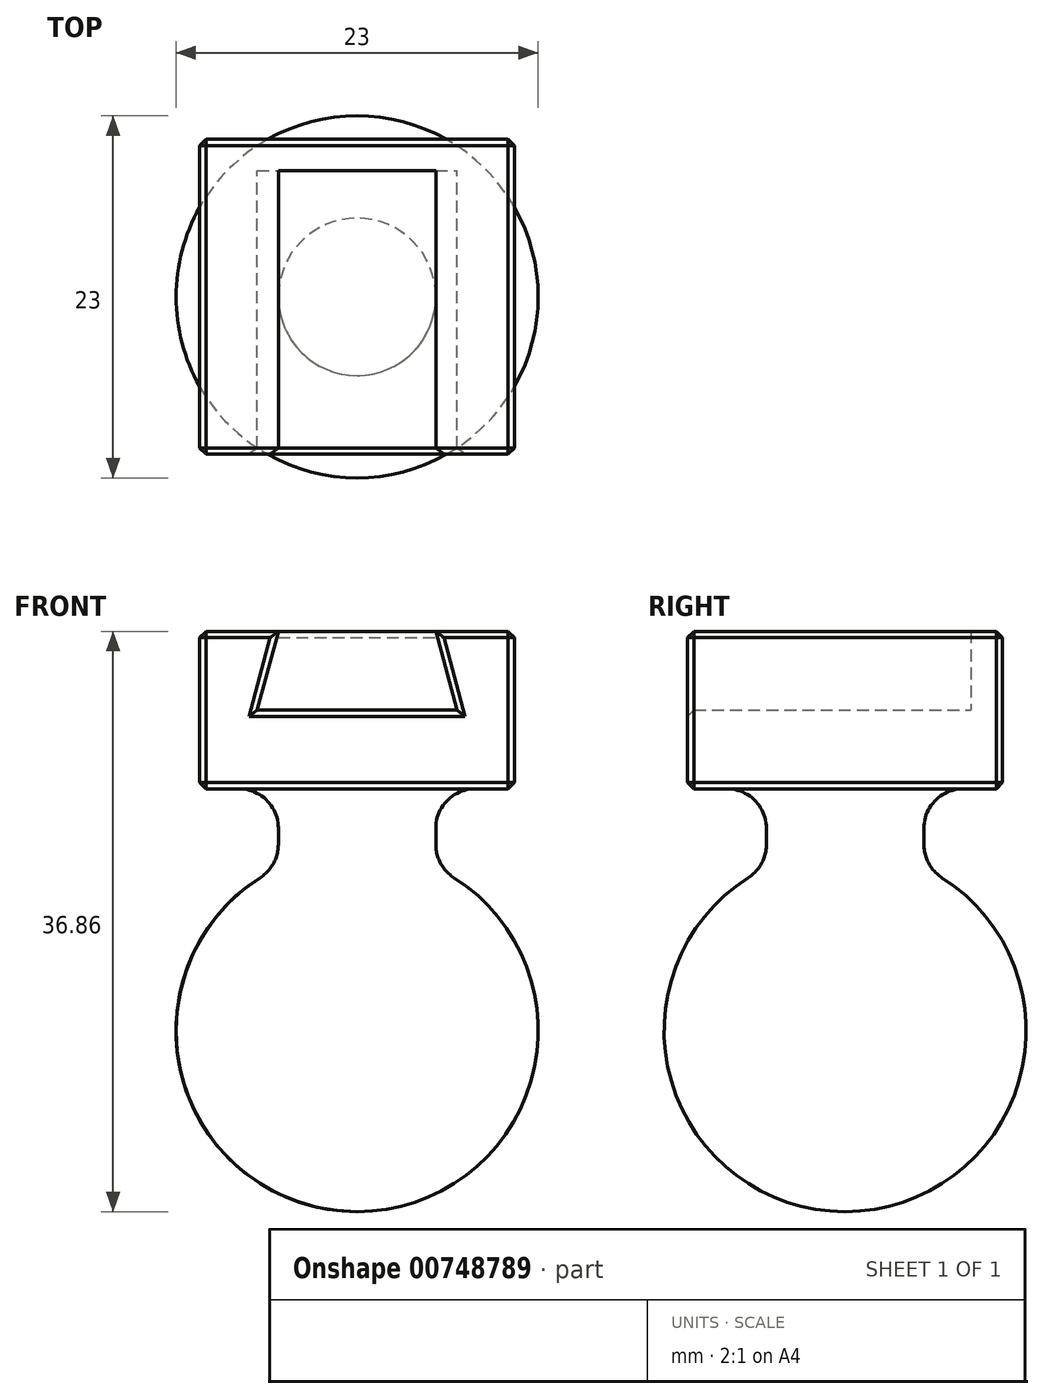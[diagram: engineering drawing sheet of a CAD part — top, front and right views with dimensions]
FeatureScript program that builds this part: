
annotation { "Feature Type Name" : "Feature", "Feature Type Description" : "" }
export const myFeature = defineFeature(function(context is Context, id is Id, definition is map)
    precondition{}
    {
        {
            assignVariable(context, id + "F0", {"name" : "PrintOffset", "anyValue" : 0.4});
        }
        {
            assignVariable(context, id + "F1", {"name" : "DovetailBackstopDepth", "anyValue" : 2});
        }
        {
            assignVariable(context, id + "F2", {"name" : "DovetailDepth", "anyValue" : 20});
        }
        {
            var Q0;
            Q0=qCreatedBy(makeId("Front.planeOp"),FACE);
            var sketch = newSketch(context, id + "F3", { "sketchPlane" : qUnion([Q0])});
            skCircle(sketch, "E0", {"center": v(0, 11.5) * mm, "radius": 11.5 * mm});
            skLineSegment(sketch, "E1", {"start": v(5, 21.86) * mm, "end": v(5, 26.86) * mm});
            skLineSegment(sketch, "E2", {"start": v(0, 26.86) * mm, "end": v(0, 62.06) * mm, "construction": true});
            skLineSegment(sketch, "E3.MirrorCS", {"start": v(-5, 21.86) * mm, "end": v(-5, 26.86) * mm});
            skLineSegment(sketch, "E4", {"start": v(-10, 26.86) * mm, "end": v(10, 26.86) * mm});
            skPoint(sketch, "E5", {"position": v(0, 26.86) * mm});
            skLineSegment(sketch, "E6", {"start": v(0, 26.86) * mm, "end": v(0, 0) * mm});
            skLineSegment(sketch, "E7", {"start": v(-6.34, 31.86) * mm, "end": v(6.34, 31.86) * mm});
            skLineSegment(sketch, "E8", {"start": v(-10, 26.86) * mm, "end": v(-10, 36.86) * mm});
            skLineSegment(sketch, "E9", {"start": v(-10, 36.86) * mm, "end": v(-5, 36.86) * mm});
            skLineSegment(sketch, "E10", {"start": v(-5, 36.86) * mm, "end": v(-6.34, 31.86) * mm});
            skLineSegment(sketch, "E11.MirrorCS", {"start": v(5, 36.86) * mm, "end": v(6.34, 31.86) * mm});
            skLineSegment(sketch, "E12.MirrorCS", {"start": v(10, 26.86) * mm, "end": v(10, 36.86) * mm});
            skLineSegment(sketch, "E13.MirrorCS", {"start": v(10, 36.86) * mm, "end": v(5, 36.86) * mm});
            skLineSegment(sketch, "E14", {"start": v(-5, 36.86) * mm, "end": v(5, 36.86) * mm});
            skSolve(sketch);
        }
        {
            var Q0;
            {var subQ2=sQuery(id+"F3.wireOp",EDGE,"E6");Q0=makeQuery(id+"F3.imprint","IMPRINT",FACE,{"disambiguationData":[TD([[makeQuery(id+"F3.imprint","IMPRINT",EDGE,{"derivedFrom":subQ2}),-1.0]])]});}
            var Q1;
            Q1=sQuery(id+"F3.wireOp",EDGE,"E6");
            revolve(context, id + "F4", {"entities" : qUnion([Q0]), "axis" : qUnion([Q1]), "revolveType" : RevolveType.FULL});
        }
        {
            var Q0;
            {var subQ0=sQuery(id+"F3.wireOp",EDGE,"E3.MirrorCS");Q0=makeQuery(id+"F3.imprint","IMPRINT",FACE,{"disambiguationData":[TD([[makeQuery(id+"F3.imprint","IMPRINT",EDGE,{"derivedFrom":subQ0}),-1.0]])]});}
            var Q1;
            Q1=sQuery(id+"F3.wireOp",EDGE,"E6");
            revolve(context, id + "F5", {"operationType" : NewBodyOperationType.ADD, "entities" : qUnion([Q0]), "axis" : qUnion([Q1]), "revolveType" : RevolveType.FULL});
        }
        {
            var Q0;
            Q0=makeQuery(id+"F3.imprint","IMPRINT",FACE,{"disambiguationData":[TD([[makeQuery(id+"F3.imprint","IMPRINT",EDGE,{"derivedFrom":sQuery(id+"F3.wireOp",EDGE,"E7")}),-1.0]])]});
            extrude(context, id + "F6", {"entities" : qUnion([Q0]), "operationType" : NewBodyOperationType.ADD, "depth" : (getVariable(context, 'DovetailDepth')) * mm, "symmetric" : true});
        }
        {
            var Q0;
            Q0=makeQuery(id+"F3.imprint","IMPRINT",FACE,{"disambiguationData":[TD([[makeQuery(id+"F3.imprint","IMPRINT",EDGE,{"derivedFrom":sQuery(id+"F3.wireOp",EDGE,"E7")}),1.0]])]});
            extrude(context, id + "F7", {"entities" : qUnion([Q0]), "operationType" : NewBodyOperationType.ADD, "oppositeDirection" : true, "depth" : (getVariable(context, 'DovetailDepth') / 2) * mm, "hasSecondDirection" : true, "secondDirectionOppositeDirection" : true, "secondDirectionDepth" : (getVariable(context, 'DovetailDepth') / 2 - getVariable(context, 'DovetailBackstopDepth')) * mm});
        }
        {
            var Q0;
            Q0=makeQuery(id+"F5.opRevolve","SWEPT_FACE",FACE,{"disambiguationData":[OSD([sQuery(id+"F3.wireOp",EDGE,"E3.MirrorCS")])]});
            fillet(context, id + "F9", {"entities" : qUnion([Q0]), "radius" : 2.5 * mm, "tangentPropagation" : true, "allowEdgeOverflow" : false});
        }
        {
            var Q0;
            Q0=makeQuery(id+"F6.opExtrude","CAP_FACE",FACE,{"disambiguationData":[OSD([sQuery(id+"F3.wireOp",EDGE,"E4"),sQuery(id+"F3.wireOp",EDGE,"E7"),sQuery(id+"F3.wireOp",EDGE,"E8"),sQuery(id+"F3.wireOp",EDGE,"E9"),sQuery(id+"F3.wireOp",EDGE,"E10"),sQuery(id+"F3.wireOp",EDGE,"E11.MirrorCS"),sQuery(id+"F3.wireOp",EDGE,"E12.MirrorCS"),sQuery(id+"F3.wireOp",EDGE,"E13.MirrorCS")])],"isStart":false});
            var Q1;
            Q1=makeQuery(id+"F6.opExtrude","SWEPT_FACE",FACE,{"disambiguationData":[OSD([sQuery(id+"F3.wireOp",EDGE,"E12.MirrorCS")])]});
            var Q2;
            Q2=makeQuery(id+"F6.opExtrude","SWEPT_FACE",FACE,{"disambiguationData":[OSD([sQuery(id+"F3.wireOp",EDGE,"E4")])]});
            var Q3;
            Q3=makeQuery(id+"F6.opExtrude","SWEPT_FACE",FACE,{"disambiguationData":[OSD([sQuery(id+"F3.wireOp",EDGE,"E8")])]});
            var Q4;
            {var subQ0=sQuery(id+"F3.wireOp",EDGE,"E11.MirrorCS");var subQ1=sQuery(id+"F3.wireOp",EDGE,"E10");var subQ2=sQuery(id+"F3.wireOp",EDGE,"E7");Q4=makeQuery(id+"F7.boolean.opBoolean","MERGE",FACE,{"derivedFrom":[makeQuery(id+"F6.opExtrude","CAP_FACE",FACE,{"disambiguationData":[OSD([sQuery(id+"F3.wireOp",EDGE,"E4"),subQ2,sQuery(id+"F3.wireOp",EDGE,"E8"),sQuery(id+"F3.wireOp",EDGE,"E9"),subQ1,subQ0,sQuery(id+"F3.wireOp",EDGE,"E12.MirrorCS"),sQuery(id+"F3.wireOp",EDGE,"E13.MirrorCS")])],"isStart":true}),makeQuery(id+"F7.opExtrude","CAP_FACE",FACE,{"disambiguationData":[OSD([subQ2,subQ1,subQ0,sQuery(id+"F3.wireOp",EDGE,"E14")])],"isStart":false})]});}
            chamfer(context, id + "F8", {"entities" : qUnion([Q0, Q1, Q2, Q3, Q4]), "width" : (getVariable(context, 'PrintOffset')) * mm, "tangentPropagation" : true});
        }
    });
